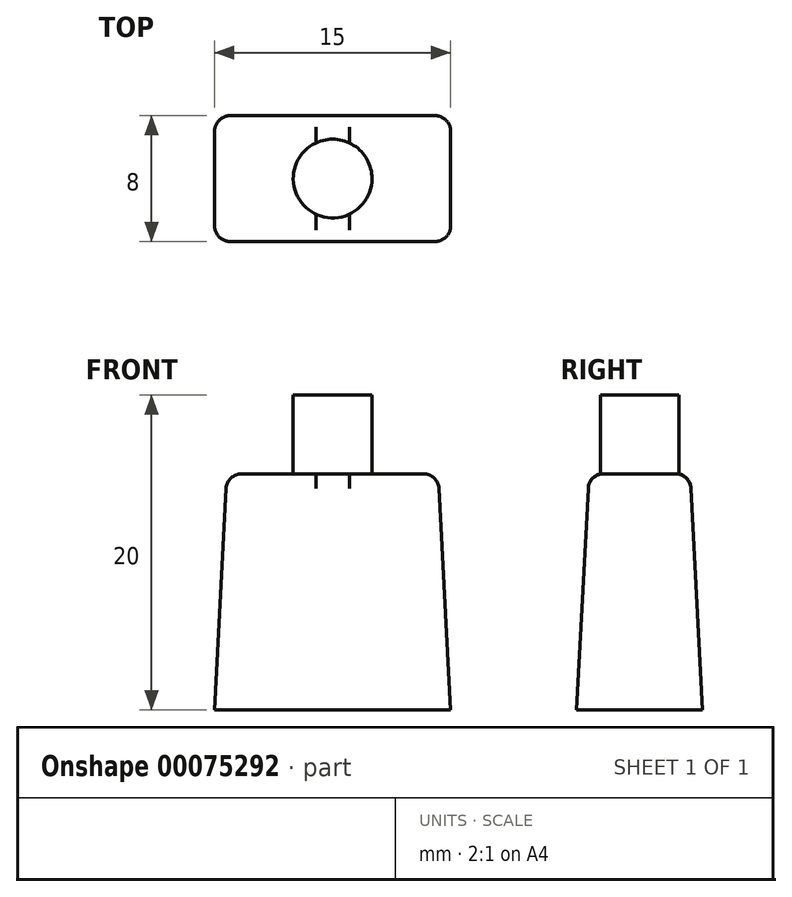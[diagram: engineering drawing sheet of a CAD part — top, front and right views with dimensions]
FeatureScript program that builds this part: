
annotation { "Feature Type Name" : "Feature", "Feature Type Description" : "" }
export const myFeature = defineFeature(function(context is Context, id is Id, definition is map)
    precondition{}
    {
        {
            var Q0;
            Q0=qCreatedBy(makeId("Top.planeOp"),FACE);
            var sketch = newSketch(context, id + "F0", { "sketchPlane" : qUnion([Q0])});
            skLineSegment(sketch, "E0.rect.bottom", {"start": v(7.5, 4) * mm, "end": v(-7.5, 4) * mm});
            skLineSegment(sketch, "E0.rect.top", {"start": v(7.5, -4) * mm, "end": v(-7.5, -4) * mm});
            skLineSegment(sketch, "E0.rect.left", {"start": v(7.5, 4) * mm, "end": v(7.5, -4) * mm});
            skLineSegment(sketch, "E0.rect.right", {"start": v(-7.5, 4) * mm, "end": v(-7.5, -4) * mm});
            skPoint(sketch, "E0.rect.middle", {"position": v(0, 0) * mm});
            skSolve(sketch);
        }
        {
            var Q0;
            Q0 = qSketchRegion(id + "F0", true);
            extrude(context, id + "F1", {"entities" : qUnion([Q0]), "depth" : 15 * mm, "hasDraft" : true, "draftAngle" : 3 * degree, "draftPullDirection" : true});
        }
        {
            var Q0;
            Q0=makeQuery(id+"F1.opExtrude","CAP_FACE",FACE,{"disambiguationData":[OSD([sQuery(id+"F0.wireOp",EDGE,"E0.rect.bottom"),sQuery(id+"F0.wireOp",EDGE,"E0.rect.top"),sQuery(id+"F0.wireOp",EDGE,"E0.rect.left"),sQuery(id+"F0.wireOp",EDGE,"E0.rect.right")])],"isStart":false});
            var sketch = newSketch(context, id + "F2", { "sketchPlane" : qUnion([Q0])});
            skCircle(sketch, "E1", {"center": v(0, 0) * mm, "radius": 2.5 * mm});
            skSolve(sketch);
        }
        {
            var Q0;
            Q0 = qSketchRegion(id + "F2", true);
            extrude(context, id + "F3", {"entities" : qUnion([Q0]), "operationType" : NewBodyOperationType.ADD, "depth" : 5 * mm});
        }
        {
            var Q0;
            Q0=makeQuery(id+"F1.opExtrude","SWEPT_EDGE",EDGE,{"disambiguationData":[OSD([sQuery(id+"F0.wireOp",EDGE,"E0.rect.top"),sQuery(id+"F0.wireOp",EDGE,"E0.rect.right")])]});
            var Q1;
            Q1=makeQuery(id+"F1.opExtrude","SWEPT_EDGE",EDGE,{"disambiguationData":[OSD([sQuery(id+"F0.wireOp",EDGE,"E0.rect.top"),sQuery(id+"F0.wireOp",EDGE,"E0.rect.left")])]});
            var Q2;
            Q2=makeQuery(id+"F1.opExtrude","SWEPT_EDGE",EDGE,{"disambiguationData":[OSD([sQuery(id+"F0.wireOp",EDGE,"E0.rect.bottom"),sQuery(id+"F0.wireOp",EDGE,"E0.rect.left")])]});
            var Q3;
            Q3=makeQuery(id+"F1.opExtrude","CAP_EDGE",EDGE,{"disambiguationData":[OSD([sQuery(id+"F0.wireOp",EDGE,"E0.rect.left")])],"isStart":false});
            var Q4;
            Q4=makeQuery(id+"F1.opExtrude","CAP_EDGE",EDGE,{"disambiguationData":[OSD([sQuery(id+"F0.wireOp",EDGE,"E0.rect.top")])],"isStart":false});
            var Q5;
            Q5=makeQuery(id+"F1.opExtrude","CAP_EDGE",EDGE,{"disambiguationData":[OSD([sQuery(id+"F0.wireOp",EDGE,"E0.rect.right")])],"isStart":false});
            var Q6;
            Q6=makeQuery(id+"F1.opExtrude","CAP_EDGE",EDGE,{"disambiguationData":[OSD([sQuery(id+"F0.wireOp",EDGE,"E0.rect.bottom")])],"isStart":false});
            var Q7;
            Q7=makeQuery(id+"F1.opExtrude","SWEPT_EDGE",EDGE,{"disambiguationData":[OSD([sQuery(id+"F0.wireOp",EDGE,"E0.rect.bottom"),sQuery(id+"F0.wireOp",EDGE,"E0.rect.right")])]});
            fillet(context, id + "F4", {"entities" : qUnion([Q0, Q1, Q2, Q3, Q4, Q5, Q6, Q7]), "radius" : 1 * mm, "tangentPropagation" : true, "allowEdgeOverflow" : false});
        }
    });
